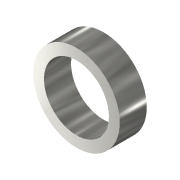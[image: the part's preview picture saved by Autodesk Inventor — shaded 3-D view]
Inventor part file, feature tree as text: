
AUTODESK INVENTOR PART (.ipt)
format: ipt  version: 2022 (Build 260153000, 153)  size: 96,768 bytes
history: native  units: mm
features: reference x2, other x2, extrude x1, sketch x1
ambient origin geometry x8: Origin, YZ Plane, XZ Plane, XY Plane, X Axis, Y Axis, Z Axis, Center Point
bodies: Volumenkörper1 (feature_tree)
feature tree (6):
  extrude  "Extrusion1"  Depth=2.5mm TaperAngle=0.0deg
  sketch  "Skizze1"  dims[d0=8.0mm d1=2.5mm d2=0.0mm]
  reference  "Referenz1"
  reference  "Referenz2"
  other  "Assembly_Cube_Template_rotational_filtermount_v3.iam"
  other  "20_Cube_Insert_rotational_filtermount_v3.iam:1"
